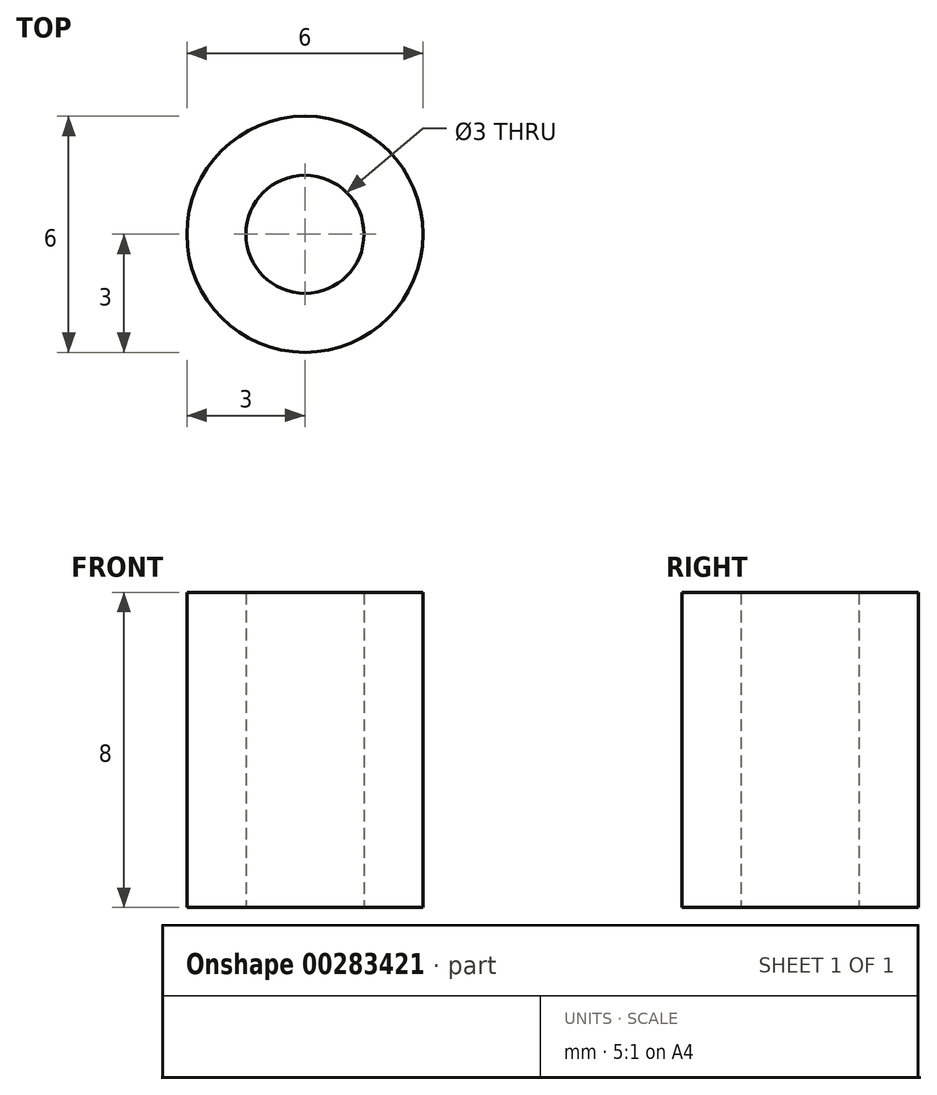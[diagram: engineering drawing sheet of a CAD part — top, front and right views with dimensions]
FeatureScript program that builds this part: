
annotation { "Feature Type Name" : "Feature", "Feature Type Description" : "" }
export const myFeature = defineFeature(function(context is Context, id is Id, definition is map)
    precondition{}
    {
        {
            var Q0;
            Q0=qCreatedBy(makeId("Top.planeOp"),FACE);
            var sketch = newSketch(context, id + "F0", { "sketchPlane" : qUnion([Q0])});
            skCircle(sketch, "E0", {"center": v(0, 0) * mm, "radius": 1.5 * mm});
            skCircle(sketch, "E1", {"center": v(0, 0) * mm, "radius": 3 * mm});
            skSolve(sketch);
        }
        {
            var Q0;
            Q0=qSketchRegion(id+"F0",true);
            extrude(context, id + "F1", {"entities" : qUnion([Q0]), "depth" : 8 * mm});
        }
    });
